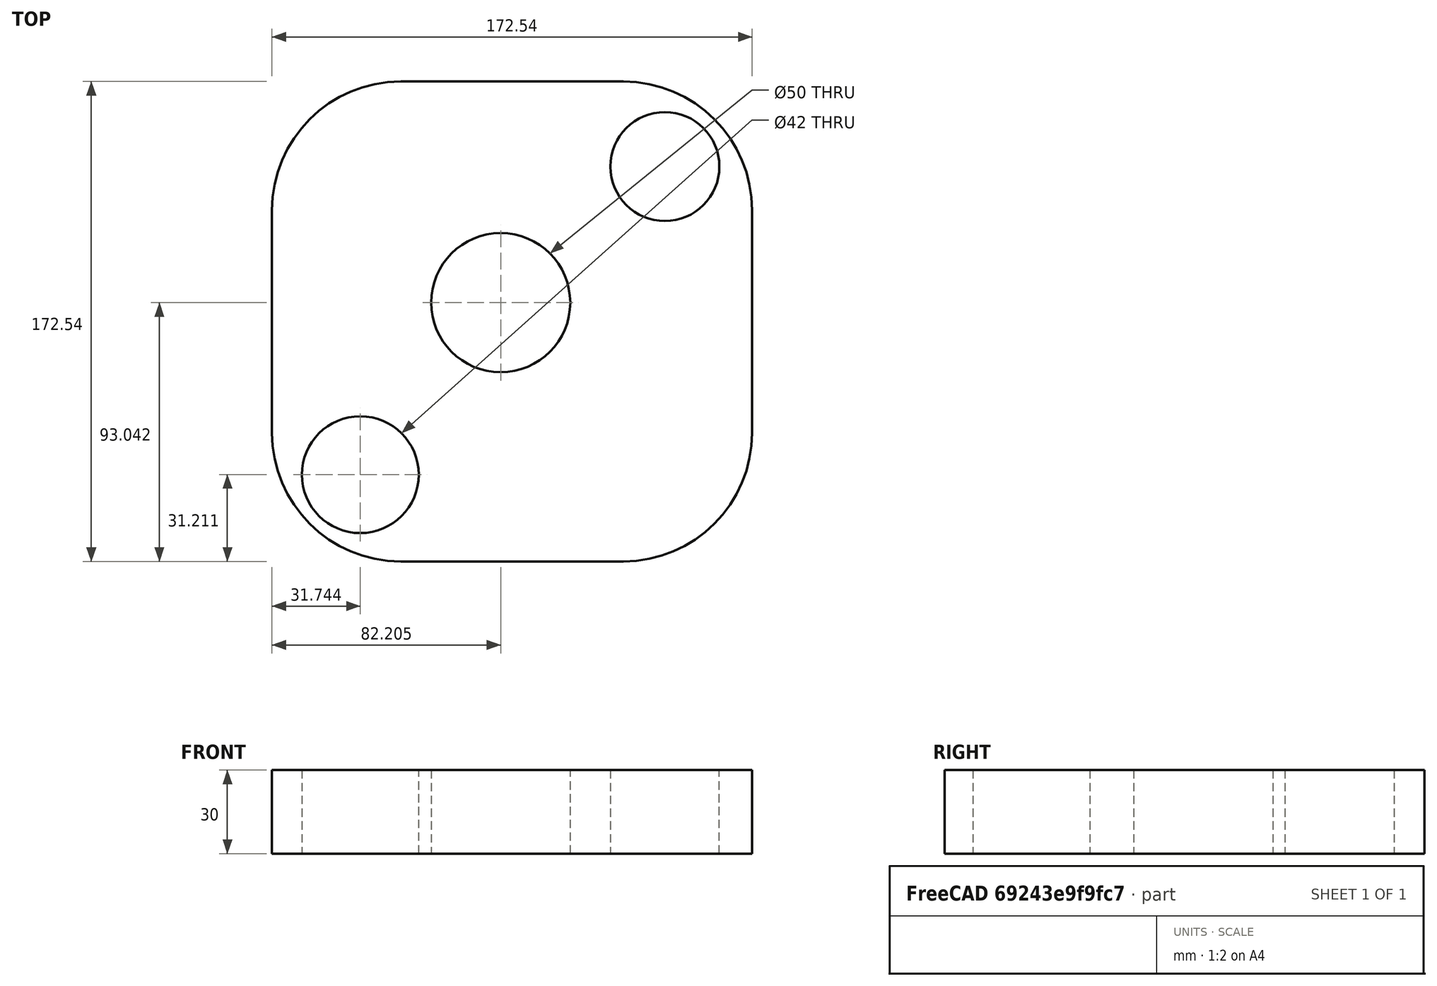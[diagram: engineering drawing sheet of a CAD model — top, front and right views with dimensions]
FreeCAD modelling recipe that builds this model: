
FCSTD DOCUMENT  (FreeCAD 0.18R16131 (Git))
Label: Momentum_Mold_Plate_1-2_160X200_12T_25mm(lm12uu)
License: All rights reserved
LicenseURL: http://en.wikipedia.org/wiki/All_rights_reserved
objects: PartDesign::Pad×2, Sketcher::SketchObject×1, PartDesign::Body×1
note: 6 computed .brp shape members not serialized (recipe doc carries the construction recipe); baked Part::Feature solids carry a one-line shape summary decoded from their .brp

FEATURE [Sketcher::SketchObject] Sketch
  MapMode = 5
  Support = -> [XY_Plane]
  sketch-geometry (11):
    g0: LineSegment StartX=-35.5842 StartY=-63.1111 StartZ=0 EndX=44.4158 EndY=-63.1111 EndZ=0
    g1: LineSegment StartX=90.685 StartY=-16.8419 StartZ=0 EndX=90.685 EndY=63.1581 EndZ=0
    g2: LineSegment StartX=44.4158 StartY=109.427 StartZ=0 EndX=-35.5842 EndY=109.427 EndZ=0
    g3: LineSegment StartX=-81.8534 StartY=63.1581 StartZ=0 EndX=-81.8534 EndY=-16.8419 EndZ=0
    g4: Circle CenterX=0.354903 CenterY=29.9322 CenterZ=0 NormalX=0 NormalY=0 NormalZ=1 AngleXU=0 Radius=25
    g5: Circle CenterX=-50.1062 CenterY=-31.8986 CenterZ=0 NormalX=0 NormalY=0 NormalZ=1 AngleXU=0 Radius=21
    g6: Circle CenterX=59.3629 CenterY=78.8583 CenterZ=0 NormalX=0 NormalY=0 NormalZ=1 AngleXU=0 Radius=19.5845
    g7: ArcOfCircle CenterX=-35.5842 CenterY=63.1581 CenterZ=0 NormalX=0 NormalY=0 NormalZ=1 AngleXU=0 Radius=46.2692 StartAngle=1.5708 EndAngle=3.14159
    g8: ArcOfCircle CenterX=44.4158 CenterY=63.1581 CenterZ=0 NormalX=0 NormalY=0 NormalZ=1 AngleXU=0 Radius=46.2692 StartAngle=1e-16 EndAngle=1.5708
    g9: ArcOfCircle CenterX=44.4158 CenterY=-16.8419 CenterZ=0 NormalX=0 NormalY=0 NormalZ=1 AngleXU=0 Radius=46.2692 StartAngle=4.71239 EndAngle=6.28319
    g10: ArcOfCircle CenterX=-35.5842 CenterY=-16.8419 CenterZ=0 NormalX=0 NormalY=0 NormalZ=1 AngleXU=0 Radius=46.2692 StartAngle=3.14159 EndAngle=4.71239
  constraints (19):
    c: Horizontal(g0)
    c: Horizontal(g2)
    c: Vertical(g1)
    c: Vertical(g3)
    c: Radius(g4) = 25
    c: Radius(g5) = 21
    c: Tangent(g2,g7) = -1.5708
    c: Tangent(g3,g7) = -1.5708
    c: Tangent(g2,g8) = -1.5708
    c: Tangent(g1,g8) = -1.5708
    c: Tangent(g1,g9) = -1.5708
    c: Tangent(g0,g9) = -1.5708
    c: Tangent(g0,g10) = -1.5708
    c: Tangent(g3,g10) = -1.5708
    c: Vertical(g7,g10)
    c: DistanceY(g1,g1) = 80
    c: DistanceY(g3,g3) = 80
    c: Horizontal(g1,g3)
    c: DistanceX(g2,g2) = 80
FEATURE [PartDesign::Pad] Pad
  Length = 30
  Length2 = 100
  Profile = -> Sketch
  Type = 0
FEATURE [PartDesign::Pad] Pad001
  BaseFeature = -> Pad
  Length = 30
  Length2 = 100
  Profile = -> Sketch
  Type = 0
FEATURE [PartDesign::Body] Body
  Group = -> [Sketch,Pad,Pad001]
  Origin = -> Origin
  Tip = -> Pad001
